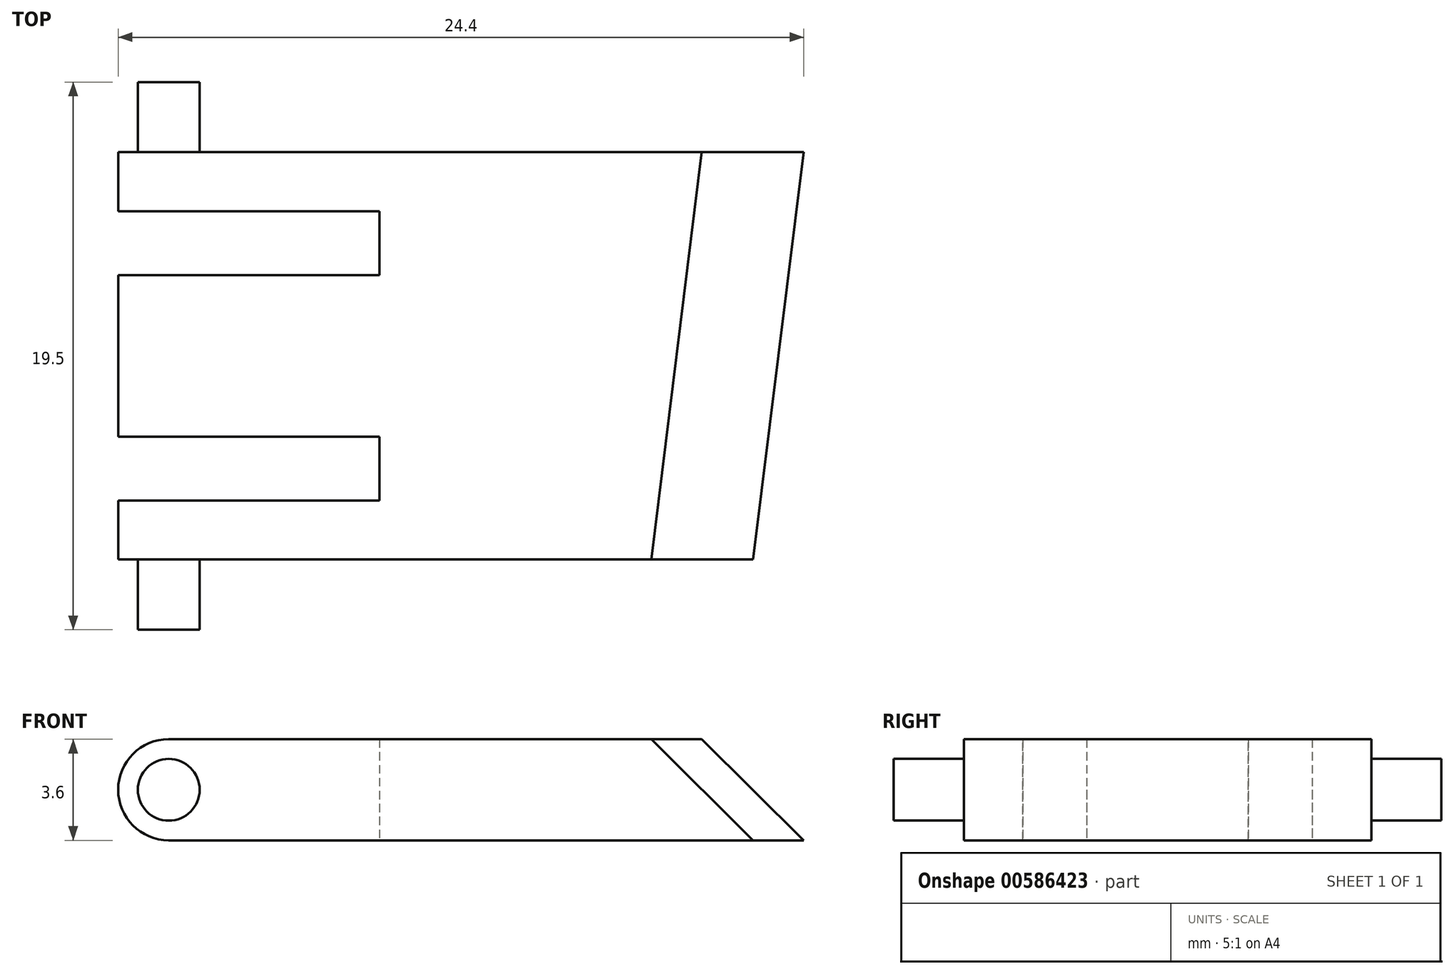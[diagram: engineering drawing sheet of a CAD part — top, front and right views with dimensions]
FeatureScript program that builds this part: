
annotation { "Feature Type Name" : "Feature", "Feature Type Description" : "" }
export const myFeature = defineFeature(function(context is Context, id is Id, definition is map)
    precondition{}
    {
        {
            var Q0;
            Q0=qCreatedBy(makeId("Top.planeOp"),FACE);
            var sketch = newSketch(context, id + "F0", { "sketchPlane" : qUnion([Q0])});
            skLineSegment(sketch, "E0", {"start": v(0, 0) * mm, "end": v(24.4, 0) * mm});
            skLineSegment(sketch, "E1", {"start": v(24.4, 0) * mm, "end": v(22.6, -14.5) * mm});
            skLineSegment(sketch, "E2", {"start": v(22.6, -14.5) * mm, "end": v(0, -14.5) * mm});
            skLineSegment(sketch, "E3", {"start": v(0, -14.5) * mm, "end": v(0, -12.4) * mm});
            skLineSegment(sketch, "E4", {"start": v(0, -12.4) * mm, "end": v(9.3, -12.4) * mm});
            skLineSegment(sketch, "E5", {"start": v(9.3, -12.4) * mm, "end": v(9.3, -10.12) * mm});
            skLineSegment(sketch, "E6", {"start": v(9.3, -10.12) * mm, "end": v(0, -10.12) * mm});
            skLineSegment(sketch, "E7", {"start": v(0, -10.12) * mm, "end": v(0, -4.37) * mm});
            skLineSegment(sketch, "E8", {"start": v(0, -4.37) * mm, "end": v(9.3, -4.37) * mm});
            skLineSegment(sketch, "E9", {"start": v(9.3, -4.37) * mm, "end": v(9.3, -2.1) * mm});
            skLineSegment(sketch, "E10", {"start": v(9.3, -2.1) * mm, "end": v(0, -2.1) * mm});
            skLineSegment(sketch, "E11", {"start": v(0, -2.1) * mm, "end": v(0, 0) * mm});
            skSolve(sketch);
        }
        {
            var Q0;
            Q0=makeQuery(id+"F0.imprint","IMPRINT",FACE,{"disambiguationData":[TD([[makeQuery(id+"F0.imprint","IMPRINT",EDGE,{"derivedFrom":sQuery(id+"F0.wireOp",EDGE,"E0")}),-1.0]])]});
            extrude(context, id + "F1", {"entities" : qUnion([Q0]), "depth" : 3.6 * mm, "offsetDistance" : 25 * mm});
        }
        {
            var Q0;
            Q0=makeQuery(id+"F1.opExtrude","CAP_EDGE",EDGE,{"disambiguationData":[OSD([sQuery(id+"F0.wireOp",EDGE,"E1")])],"isStart":false});
            chamfer(context, id + "F2", {"entities" : qUnion([Q0]), "chamferType" : ChamferType.OFFSET_ANGLE, "width" : 3.6 * mm, "oppositeDirection" : false, "angle" : 45 * degree});
        }
        {
            var Q0;
            Q0=makeQuery(id+"F1.opExtrude","CAP_EDGE",EDGE,{"disambiguationData":[OSD([sQuery(id+"F0.wireOp",EDGE,"E7")])],"isStart":false});
            fillet(context, id + "F3", {"entities" : qUnion([Q0]), "radius" : 1.8 * mm, "tangentPropagation" : true, "allowEdgeOverflow" : false});
        }
        {
            var Q0;
            Q0=makeQuery(id+"F1.opExtrude","CAP_EDGE",EDGE,{"disambiguationData":[OSD([sQuery(id+"F0.wireOp",EDGE,"E7")])],"isStart":true});
            fillet(context, id + "F4", {"entities" : qUnion([Q0]), "radius" : 1.8 * mm, "tangentPropagation" : true, "allowEdgeOverflow" : false});
        }
        {
            var Q0;
            Q0=makeQuery(id+"F1.opExtrude","CAP_EDGE",EDGE,{"disambiguationData":[OSD([sQuery(id+"F0.wireOp",EDGE,"E3")])],"isStart":false});
            fillet(context, id + "F5", {"entities" : qUnion([Q0]), "radius" : 1.8 * mm, "tangentPropagation" : true, "allowEdgeOverflow" : false});
        }
        {
            var Q0;
            Q0=makeQuery(id+"F1.opExtrude","CAP_EDGE",EDGE,{"disambiguationData":[OSD([sQuery(id+"F0.wireOp",EDGE,"E3")])],"isStart":true});
            fillet(context, id + "F6", {"entities" : qUnion([Q0]), "radius" : 1.8 * mm, "tangentPropagation" : true, "allowEdgeOverflow" : false});
        }
        {
            var Q0;
            Q0=makeQuery(id+"F1.opExtrude","CAP_EDGE",EDGE,{"disambiguationData":[OSD([sQuery(id+"F0.wireOp",EDGE,"E11")])],"isStart":false});
            fillet(context, id + "F7", {"entities" : qUnion([Q0]), "radius" : 1.8 * mm, "tangentPropagation" : true, "allowEdgeOverflow" : false});
        }
        {
            var Q0;
            Q0=makeQuery(id+"F1.opExtrude","CAP_EDGE",EDGE,{"disambiguationData":[OSD([sQuery(id+"F0.wireOp",EDGE,"E11")])],"isStart":true});
            fillet(context, id + "F8", {"entities" : qUnion([Q0]), "radius" : 1.8 * mm, "tangentPropagation" : true, "allowEdgeOverflow" : false});
        }
        {
            var Q0;
            Q0=makeQuery(id+"F1.opExtrude","SWEPT_FACE",FACE,{"disambiguationData":[OSD([sQuery(id+"F0.wireOp",EDGE,"E2")])]});
            var sketch = newSketch(context, id + "F9", { "sketchPlane" : qUnion([Q0])});
            skCircle(sketch, "E12", {"center": v(1.8, 1.8) * mm, "radius": 1.1 * mm});
            skSolve(sketch);
        }
        {
            var Q0;
            Q0=makeQuery(id+"F9.imprint","IMPRINT",FACE,{"disambiguationData":[TD([[makeQuery(id+"F9.imprint","IMPRINT",EDGE,{"derivedFrom":sQuery(id+"F9.wireOp",EDGE,"E12")}),1.0]])]});
            extrude(context, id + "F10", {"entities" : qUnion([Q0]), "operationType" : NewBodyOperationType.ADD, "depth" : 2.5 * mm, "offsetDistance" : 25 * mm});
        }
        {
            var Q0;
            Q0=makeQuery(id+"F1.opExtrude","SWEPT_FACE",FACE,{"disambiguationData":[OSD([sQuery(id+"F0.wireOp",EDGE,"E0")])]});
            var sketch = newSketch(context, id + "F11", { "sketchPlane" : qUnion([Q0])});
            skCircle(sketch, "E13", {"center": v(-1.8, 1.8) * mm, "radius": 1.1 * mm});
            skSolve(sketch);
        }
        {
            var Q0;
            Q0=makeQuery(id+"F11.imprint","IMPRINT",FACE,{"disambiguationData":[TD([[makeQuery(id+"F11.imprint","IMPRINT",EDGE,{"derivedFrom":sQuery(id+"F11.wireOp",EDGE,"E13")}),1.0]])]});
            extrude(context, id + "F12", {"entities" : qUnion([Q0]), "operationType" : NewBodyOperationType.ADD, "depth" : 2.5 * mm, "offsetDistance" : 25 * mm});
        }
    });
